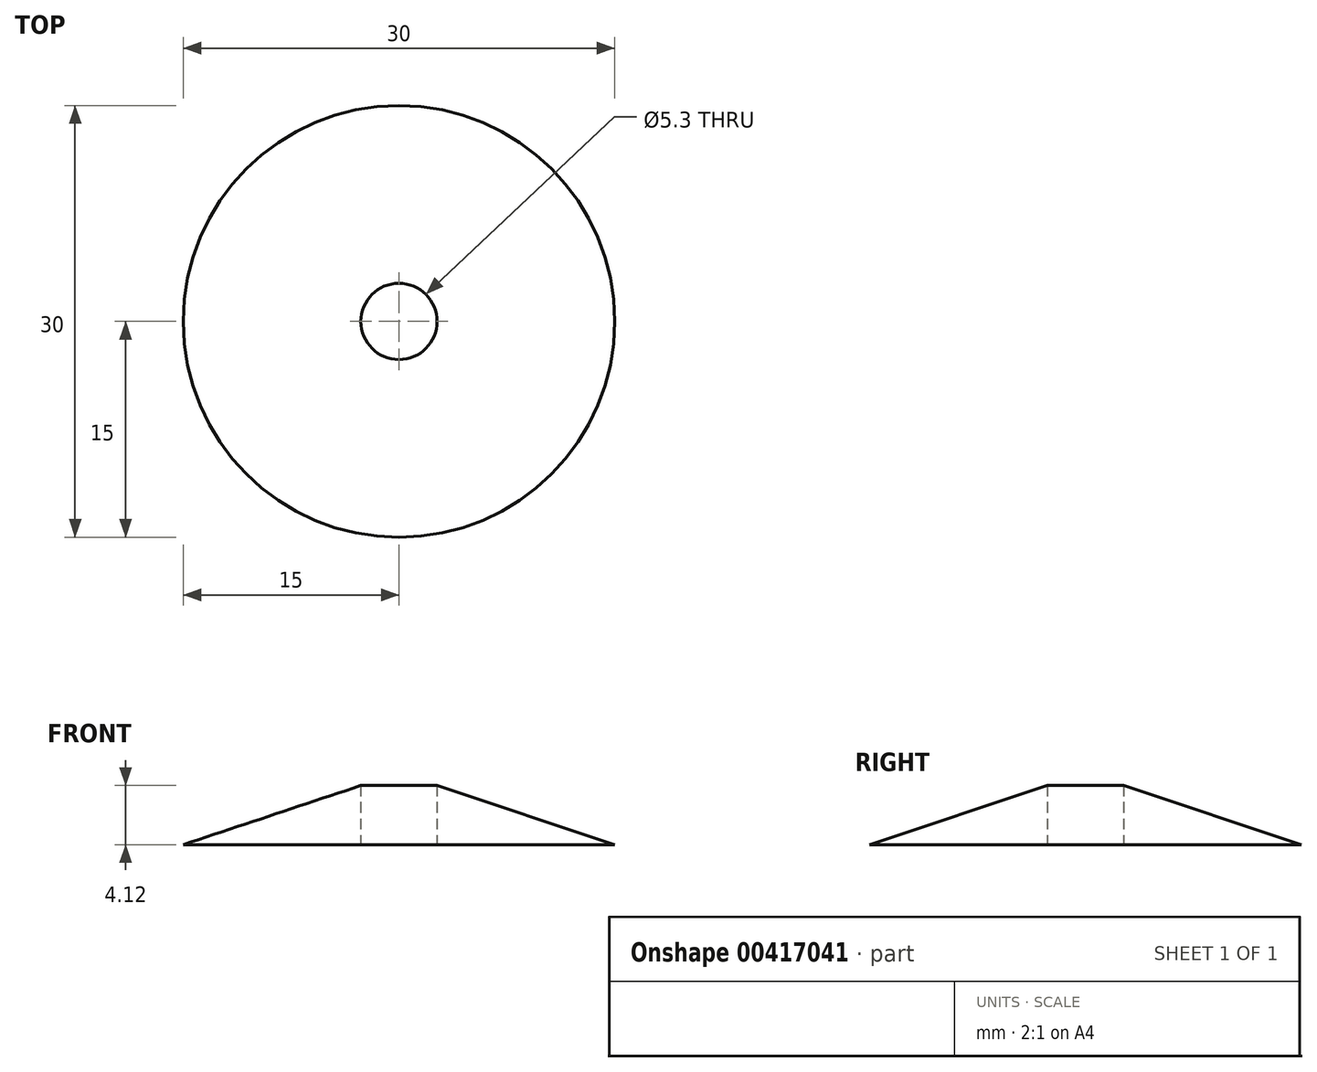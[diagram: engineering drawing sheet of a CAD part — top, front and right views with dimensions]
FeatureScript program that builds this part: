
annotation { "Feature Type Name" : "Feature", "Feature Type Description" : "" }
export const myFeature = defineFeature(function(context is Context, id is Id, definition is map)
    precondition{}
    {
        {
            var Q0;
            Q0=qCreatedBy(makeId("Front.planeOp"),FACE);
            var sketch = newSketch(context, id + "F0", { "sketchPlane" : qUnion([Q0])});
            skLineSegment(sketch, "E0", {"start": v(0, 0) * mm, "end": v(15, 0) * mm});
            skLineSegment(sketch, "E1", {"start": v(15, 0) * mm, "end": v(0, 5) * mm});
            skLineSegment(sketch, "E2", {"start": v(0, 5) * mm, "end": v(0, 0) * mm});
            skSolve(sketch);
        }
        {
            var Q0;
            Q0 = qSketchRegion(id + "F0", true);
            var Q1;
            Q1=sQuery(id+"F0.wireOp",EDGE,"E2");
            revolve(context, id + "F1", {"entities" : qUnion([Q0]), "axis" : qUnion([Q1]), "revolveType" : RevolveType.FULL});
        }
        {
            var Q0;
            Q0=makeQuery(id+"F1.opRevolve","SWEPT_FACE",FACE,{"disambiguationData":[OSD([sQuery(id+"F0.wireOp",EDGE,"E0")])]});
            var sketch = newSketch(context, id + "F2", { "sketchPlane" : qUnion([Q0])});
            skCircle(sketch, "E3", {"center": v(0, 0) * mm, "radius": 2.65 * mm});
            skSolve(sketch);
        }
        {
            var Q0;
            Q0 = qSketchRegion(id + "F2", true);
            var Q1;
            Q1=makeQuery(id+"F1.opRevolve","SWEPT_VERTEX",VERTEX,{"disambiguationData":[OSD([sQuery(id+"F0.wireOp",EDGE,"E1"),sQuery(id+"F0.wireOp",EDGE,"E2")])]});
            extrude(context, id + "F3", {"entities" : qUnion([Q0]), "operationType" : NewBodyOperationType.REMOVE, "endBound" : BoundingType.UP_TO_VERTEX, "oppositeDirection" : true, "endBoundEntityVertex" : qUnion([Q1]), "depth" : 25 * mm});
        }
    });
